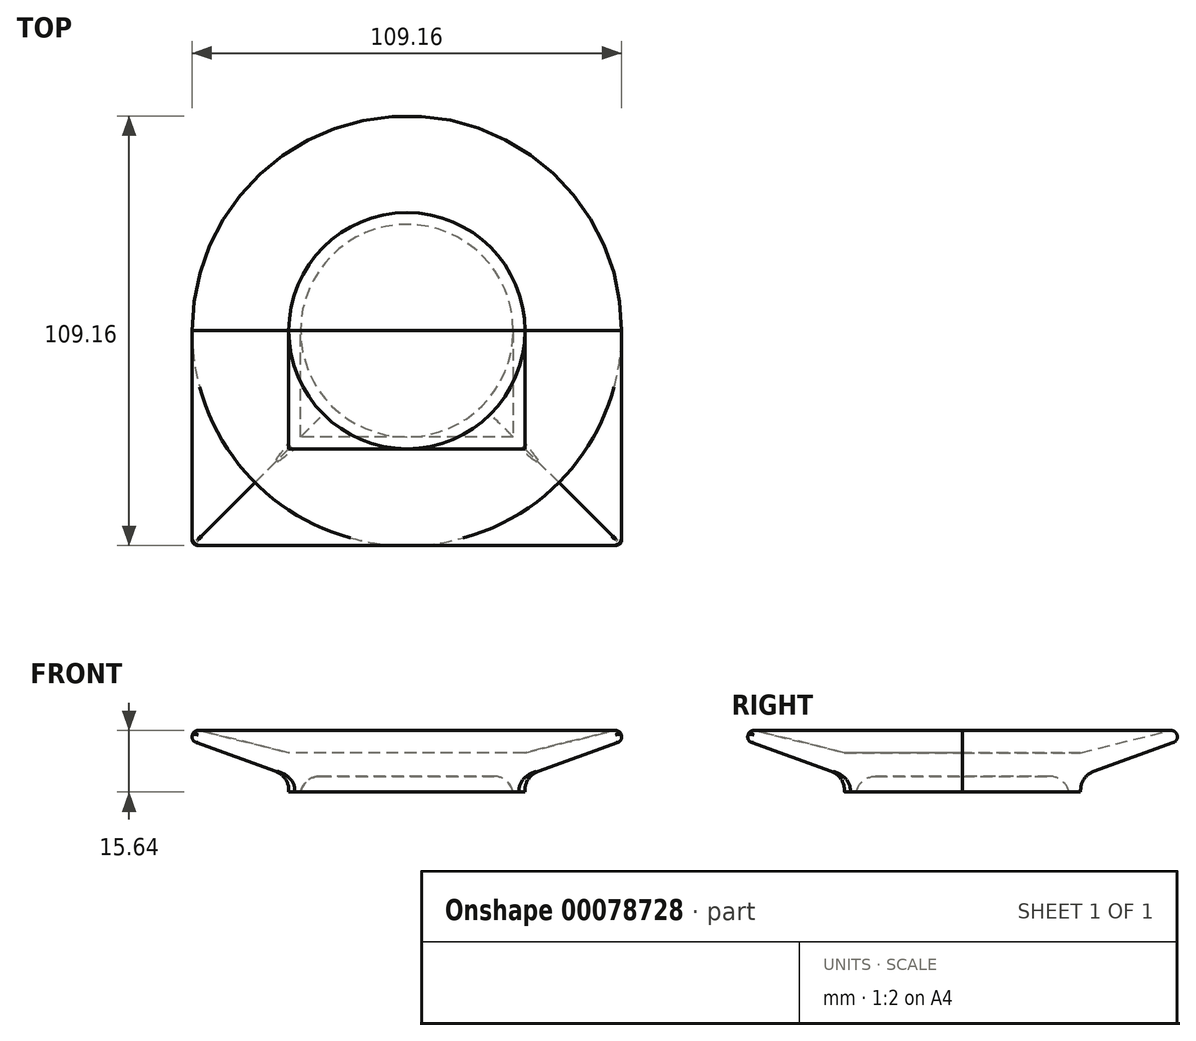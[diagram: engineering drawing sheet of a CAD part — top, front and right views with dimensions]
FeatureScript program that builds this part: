
annotation { "Feature Type Name" : "Feature", "Feature Type Description" : "" }
export const myFeature = defineFeature(function(context is Context, id is Id, definition is map)
    precondition{}
    {
        {
            var Q0;
            Q0=qCreatedBy(makeId("Top.planeOp"),FACE);
            var sketch = newSketch(context, id + "F0", { "sketchPlane" : qUnion([Q0])});
            skLineSegment(sketch, "E0.bottom", {"start": v(30, 30) * mm, "end": v(-30, 30) * mm});
            skLineSegment(sketch, "E0.top", {"start": v(30, -30) * mm, "end": v(-30, -30) * mm});
            skLineSegment(sketch, "E0.left", {"start": v(30, 30) * mm, "end": v(30, -30) * mm});
            skLineSegment(sketch, "E0.right", {"start": v(-30, 30) * mm, "end": v(-30, -30) * mm});
            skPoint(sketch, "E0.middle", {"position": v(0, 0) * mm});
            skSolve(sketch);
        }
        {
            var Q0;
            Q0=makeQuery(id+"F0.imprint","IMPRINT",FACE,{"disambiguationData":[TD([[makeQuery(id+"F0.imprint","IMPRINT",EDGE,{"derivedFrom":sQuery(id+"F0.wireOp",EDGE,"E0.bottom")}),1.0]])]});
            extrude(context, id + "F1", {"entities" : qUnion([Q0]), "depth" : 6 * mm});
        }
        {
            var Q0;
            Q0=qCreatedBy(makeId("Front.planeOp"),FACE);
            var sketch = newSketch(context, id + "F2", { "sketchPlane" : qUnion([Q0])});
            skLineSegment(sketch, "E1.0", {"start": v(30, 6) * mm, "end": v(30, 0) * mm});
            skLineSegment(sketch, "E2", {"start": v(30, 0) * mm, "end": v(55, 0) * mm, "construction": true});
            skLineSegment(sketch, "E3", {"start": v(30, 0) * mm, "end": v(55, 9.1) * mm});
            skLineSegment(sketch, "E4", {"start": v(55, 9.1) * mm, "end": v(53.97, 11.92) * mm});
            skLineSegment(sketch, "E5", {"start": v(53.97, 11.92) * mm, "end": v(30, 6) * mm});
            skLineSegment(sketch, "E6", {"start": v(0, 58.89) * mm, "end": v(0, -59.83) * mm});
            skSolve(sketch);
        }
        {
            var Q0;
            Q0=makeQuery(id+"F2.imprint","IMPRINT",FACE,{"disambiguationData":[TD([[makeQuery(id+"F2.imprint","IMPRINT",EDGE,{"derivedFrom":sQuery(id+"F2.wireOp",EDGE,"E1.0")}),1.0]])]});
            extrude(context, id + "F3", {"entities" : qUnion([Q0]), "endBound" : BoundingType.SYMMETRIC, "depth" : 122.42 * mm});
        }
        {
            var Q0;
            Q0=makeQuery(id+"F3.opExtrude","SWEPT_BODY",BODY,{"disambiguationData":[OSD([sQuery(id+"F2.wireOp",EDGE,"E1.0"),sQuery(id+"F2.wireOp",EDGE,"E3"),sQuery(id+"F2.wireOp",EDGE,"E4"),sQuery(id+"F2.wireOp",EDGE,"E5")])]});
            var Q1;
            Q1=sQuery(id+"F2.wireOp",EDGE,"E6");
            circularPattern(context, id + "F4", {"operationType" : NewBodyOperationType.ADD, "entities" : qUnion([Q0]), "axis" : qUnion([Q1]), "angle" : 360 * degree, "instanceCount" : 4, "equalSpace" : true});
        }
        {
            var Q0;
            Q0=qCreatedBy(makeId("Front.planeOp"),FACE);
            var sketch = newSketch(context, id + "F5", { "sketchPlane" : qUnion([Q0])});
            skLineSegment(sketch, "E7.0", {"start": v(30, 0) * mm, "end": v(55, 9.1) * mm});
            skLineSegment(sketch, "E8.0", {"start": v(55, 9.1) * mm, "end": v(53.97, 11.92) * mm});
            skLineSegment(sketch, "E9", {"start": v(53.97, 11.92) * mm, "end": v(62.12, 21.43) * mm});
            skLineSegment(sketch, "E10", {"start": v(62.12, 21.43) * mm, "end": v(87.77, -20) * mm});
            skLineSegment(sketch, "E11", {"start": v(87.77, -20) * mm, "end": v(30.92, -15.49) * mm});
            skLineSegment(sketch, "E12", {"start": v(30.92, -15.49) * mm, "end": v(30, 0) * mm});
            skSolve(sketch);
        }
        {
            var Q0;
            Q0=makeQuery(id+"F5.imprint","IMPRINT",FACE,{"disambiguationData":[TD([[makeQuery(id+"F5.imprint","IMPRINT",EDGE,{"derivedFrom":sQuery(id+"F5.wireOp",EDGE,"E7.0")}),-1.0]])]});
            extrude(context, id + "F6", {"entities" : qUnion([Q0]), "endBound" : BoundingType.SYMMETRIC, "depth" : 220.76 * mm});
        }
        {
            var Q0;
            Q0=makeQuery(id+"F6.opExtrude","SWEPT_BODY",BODY,{"disambiguationData":[OSD([sQuery(id+"F5.wireOp",EDGE,"E7.0"),sQuery(id+"F5.wireOp",EDGE,"E8.0"),sQuery(id+"F5.wireOp",EDGE,"E9"),sQuery(id+"F5.wireOp",EDGE,"E10"),sQuery(id+"F5.wireOp",EDGE,"E11"),sQuery(id+"F5.wireOp",EDGE,"E12")])]});
            var Q1;
            Q1=sQuery(id+"F2.wireOp",EDGE,"E6");
            circularPattern(context, id + "F7", {"operationType" : NewBodyOperationType.REMOVE, "entities" : qUnion([Q0]), "axis" : qUnion([Q1]), "angle" : 360 * degree, "instanceCount" : 4, "equalSpace" : true});
        }
        {
            var Q0;
            Q0=makeQuery(id+"F1.opExtrude","CAP_FACE",FACE,{"disambiguationData":[OSD([sQuery(id+"F0.wireOp",EDGE,"E0.bottom"),sQuery(id+"F0.wireOp",EDGE,"E0.top"),sQuery(id+"F0.wireOp",EDGE,"E0.left"),sQuery(id+"F0.wireOp",EDGE,"E0.right")])],"isStart":true});
            var sketch = newSketch(context, id + "F8", { "sketchPlane" : qUnion([Q0])});
            skLineSegment(sketch, "E13.0.0", {"start": v(-30, -30) * mm, "end": v(30, -30) * mm});
            skLineSegment(sketch, "E13.0.2", {"start": v(30, -30) * mm, "end": v(30, 30) * mm});
            skLineSegment(sketch, "E13.0.4", {"start": v(30, 30) * mm, "end": v(-30, 30) * mm});
            skLineSegment(sketch, "E13.0.6", {"start": v(-30, 30) * mm, "end": v(-30, -30) * mm});
            skLineSegment(sketch, "E14.0", {"start": v(-27, -27) * mm, "end": v(27, -27) * mm});
            skLineSegment(sketch, "E14.1", {"start": v(-27, 27) * mm, "end": v(-27, -27) * mm});
            skLineSegment(sketch, "E14.2", {"start": v(27, 27) * mm, "end": v(-27, 27) * mm});
            skLineSegment(sketch, "E14.3", {"start": v(27, -27) * mm, "end": v(27, 27) * mm});
            skPoint(sketch, "E15.orphan", {"position": v(30, 43.49) * mm});
            skPoint(sketch, "E16.orphan", {"position": v(-43.49, 30) * mm});
            skPoint(sketch, "E17.orphan", {"position": v(-30, -43.49) * mm});
            skPoint(sketch, "E18.orphan", {"position": v(-43.49, -30) * mm});
            skPoint(sketch, "E19.orphan", {"position": v(-30, -45.08) * mm});
            skPoint(sketch, "E20.orphan", {"position": v(43.49, -30) * mm});
            skPoint(sketch, "E21.orphan", {"position": v(45.17, -30) * mm});
            skSolve(sketch);
        }
        {
            var Q0;
            Q0=makeQuery(id+"F8.imprint","IMPRINT",FACE,{"disambiguationData":[TD([[makeQuery(id+"F8.imprint","IMPRINT",EDGE,{"derivedFrom":sQuery(id+"F8.wireOp",EDGE,"E13.0.0")}),-1.0]])]});
            extrude(context, id + "F9", {"entities" : qUnion([Q0]), "operationType" : NewBodyOperationType.ADD, "depth" : 4 * mm});
        }
        {
            var Q0;
            {var subQ0=sQuery(id+"F2.wireOp",EDGE,"E5");var subQ1=makeQuery(id+"F3.opExtrude","SWEPT_FACE",FACE,{"disambiguationData":[OSD([subQ0])]});var subQ2=sQuery(id+"F2.wireOp",EDGE,"E4");var subQ3=makeQuery(id+"F3.opExtrude","SWEPT_FACE",FACE,{"disambiguationData":[OSD([subQ2])]});Q0=makeQuery(id+"F4.boolean.opBoolean","SPLIT",EDGE,{"disambiguationData":[TD([subQ3,subQ1,makeQuery(id+"F4.opPattern","COPY",FACE,{"derivedFrom":subQ3,"instanceName":"1"}),makeQuery(id+"F4.opPattern","COPY",FACE,{"derivedFrom":subQ1,"instanceName":"1"}),makeQuery(id+"F4.opPattern","COPY",FACE,{"derivedFrom":subQ3,"instanceName":"2"}),makeQuery(id+"F4.opPattern","COPY",FACE,{"derivedFrom":subQ1,"instanceName":"2"})])],"derivedFrom":makeQuery(id+"F4.opPattern","COPY",EDGE,{"derivedFrom":makeQuery(id+"F3.opExtrude","SWEPT_EDGE",EDGE,{"disambiguationData":[OSD([subQ2,subQ0])]}),"instanceName":"1"})});}
            var Q1;
            {var subQ0=sQuery(id+"F2.wireOp",EDGE,"E5");var subQ1=makeQuery(id+"F3.opExtrude","SWEPT_FACE",FACE,{"disambiguationData":[OSD([subQ0])]});var subQ2=sQuery(id+"F2.wireOp",EDGE,"E4");var subQ3=makeQuery(id+"F3.opExtrude","SWEPT_FACE",FACE,{"disambiguationData":[OSD([subQ2])]});Q1=makeQuery(id+"F4.boolean.opBoolean","SPLIT",EDGE,{"disambiguationData":[TD([makeQuery(id+"F4.opPattern","COPY",FACE,{"derivedFrom":subQ3,"instanceName":"1"}),makeQuery(id+"F4.opPattern","COPY",FACE,{"derivedFrom":subQ1,"instanceName":"1"}),makeQuery(id+"F4.opPattern","COPY",FACE,{"derivedFrom":subQ3,"instanceName":"2"}),makeQuery(id+"F4.opPattern","COPY",FACE,{"derivedFrom":subQ1,"instanceName":"2"}),makeQuery(id+"F4.opPattern","COPY",FACE,{"derivedFrom":subQ3,"instanceName":"3"}),makeQuery(id+"F4.opPattern","COPY",FACE,{"derivedFrom":subQ1,"instanceName":"3"})])],"derivedFrom":makeQuery(id+"F4.opPattern","COPY",EDGE,{"derivedFrom":makeQuery(id+"F3.opExtrude","SWEPT_EDGE",EDGE,{"disambiguationData":[OSD([subQ2,subQ0])]}),"instanceName":"2"})});}
            var Q2;
            {var subQ0=sQuery(id+"F2.wireOp",EDGE,"E5");var subQ1=makeQuery(id+"F3.opExtrude","SWEPT_FACE",FACE,{"disambiguationData":[OSD([subQ0])]});var subQ2=sQuery(id+"F2.wireOp",EDGE,"E4");var subQ3=makeQuery(id+"F3.opExtrude","SWEPT_FACE",FACE,{"disambiguationData":[OSD([subQ2])]});Q2=makeQuery(id+"F4.boolean.opBoolean","SPLIT",EDGE,{"disambiguationData":[TD([subQ3,subQ1,makeQuery(id+"F4.opPattern","COPY",FACE,{"derivedFrom":subQ3,"instanceName":"2"}),makeQuery(id+"F4.opPattern","COPY",FACE,{"derivedFrom":subQ1,"instanceName":"2"}),makeQuery(id+"F4.opPattern","COPY",FACE,{"derivedFrom":subQ3,"instanceName":"3"}),makeQuery(id+"F4.opPattern","COPY",FACE,{"derivedFrom":subQ1,"instanceName":"3"})])],"derivedFrom":makeQuery(id+"F4.opPattern","COPY",EDGE,{"derivedFrom":makeQuery(id+"F3.opExtrude","SWEPT_EDGE",EDGE,{"disambiguationData":[OSD([subQ2,subQ0])]}),"instanceName":"3"})});}
            var Q3;
            {var subQ0=sQuery(id+"F2.wireOp",EDGE,"E5");var subQ1=makeQuery(id+"F3.opExtrude","SWEPT_FACE",FACE,{"disambiguationData":[OSD([subQ0])]});var subQ2=sQuery(id+"F2.wireOp",EDGE,"E4");var subQ3=makeQuery(id+"F3.opExtrude","SWEPT_FACE",FACE,{"disambiguationData":[OSD([subQ2])]});Q3=makeQuery(id+"F4.boolean.opBoolean","SPLIT",EDGE,{"disambiguationData":[TD([subQ3,subQ1,makeQuery(id+"F4.opPattern","COPY",FACE,{"derivedFrom":subQ3,"instanceName":"1"}),makeQuery(id+"F4.opPattern","COPY",FACE,{"derivedFrom":subQ1,"instanceName":"1"}),makeQuery(id+"F4.opPattern","COPY",FACE,{"derivedFrom":subQ3,"instanceName":"3"}),makeQuery(id+"F4.opPattern","COPY",FACE,{"derivedFrom":subQ1,"instanceName":"3"})])],"derivedFrom":makeQuery(id+"F3.opExtrude","SWEPT_EDGE",EDGE,{"disambiguationData":[OSD([subQ2,subQ0])]})});}
            var Q4;
            {var subQ0=makeQuery(id+"F3.opExtrude","SWEPT_FACE",FACE,{"disambiguationData":[OSD([sQuery(id+"F2.wireOp",EDGE,"E5")])]});var subQ1=sQuery(id+"F2.wireOp",EDGE,"E3");var subQ2=sQuery(id+"F2.wireOp",EDGE,"E4");Q4=makeQuery(id+"F7.boolean.opBoolean","MERGE",EDGE,{"derivedFrom":[makeQuery(id+"F4.boolean.opBoolean","SPLIT",EDGE,{"disambiguationData":[TD([makeQuery(id+"F4.opPattern","COPY",FACE,{"derivedFrom":subQ0,"instanceName":"1"})])],"derivedFrom":makeQuery(id+"F4.opPattern","COPY",EDGE,{"derivedFrom":makeQuery(id+"F3.opExtrude","SWEPT_EDGE",EDGE,{"disambiguationData":[OSD([subQ1,subQ2])]}),"instanceName":"2"})}),makeQuery(id+"F7.opPattern","COPY",EDGE,{"derivedFrom":makeQuery(id+"F6.opExtrude","SWEPT_EDGE",EDGE,{"disambiguationData":[OSD([sQuery(id+"F5.wireOp",EDGE,"E7.0"),sQuery(id+"F5.wireOp",EDGE,"E8.0")])]}),"instanceName":"2"})]});}
            var Q5;
            {var subQ0=makeQuery(id+"F3.opExtrude","SWEPT_FACE",FACE,{"disambiguationData":[OSD([sQuery(id+"F2.wireOp",EDGE,"E5")])]});var subQ1=sQuery(id+"F2.wireOp",EDGE,"E3");var subQ2=sQuery(id+"F2.wireOp",EDGE,"E4");Q5=makeQuery(id+"F7.boolean.opBoolean","MERGE",EDGE,{"derivedFrom":[makeQuery(id+"F4.boolean.opBoolean","SPLIT",EDGE,{"disambiguationData":[TD([subQ0])],"derivedFrom":makeQuery(id+"F4.opPattern","COPY",EDGE,{"derivedFrom":makeQuery(id+"F3.opExtrude","SWEPT_EDGE",EDGE,{"disambiguationData":[OSD([subQ1,subQ2])]}),"instanceName":"1"})}),makeQuery(id+"F7.opPattern","COPY",EDGE,{"derivedFrom":makeQuery(id+"F6.opExtrude","SWEPT_EDGE",EDGE,{"disambiguationData":[OSD([sQuery(id+"F5.wireOp",EDGE,"E7.0"),sQuery(id+"F5.wireOp",EDGE,"E8.0")])]}),"instanceName":"1"})]});}
            var Q6;
            {var subQ0=sQuery(id+"F2.wireOp",EDGE,"E3");var subQ1=sQuery(id+"F2.wireOp",EDGE,"E4");var subQ2=makeQuery(id+"F3.opExtrude","SWEPT_FACE",FACE,{"disambiguationData":[OSD([sQuery(id+"F2.wireOp",EDGE,"E5")])]});Q6=makeQuery(id+"F7.boolean.opBoolean","MERGE",EDGE,{"derivedFrom":[makeQuery(id+"F4.boolean.opBoolean","SPLIT",EDGE,{"disambiguationData":[TD([makeQuery(id+"F4.opPattern","COPY",FACE,{"derivedFrom":subQ2,"instanceName":"1"})])],"derivedFrom":makeQuery(id+"F3.opExtrude","SWEPT_EDGE",EDGE,{"disambiguationData":[OSD([subQ0,subQ1])]})}),makeQuery(id+"F6.opExtrude","SWEPT_EDGE",EDGE,{"disambiguationData":[OSD([sQuery(id+"F5.wireOp",EDGE,"E7.0"),sQuery(id+"F5.wireOp",EDGE,"E8.0")])]})]});}
            var Q7;
            {var subQ0=makeQuery(id+"F3.opExtrude","SWEPT_FACE",FACE,{"disambiguationData":[OSD([sQuery(id+"F2.wireOp",EDGE,"E5")])]});var subQ1=sQuery(id+"F2.wireOp",EDGE,"E3");var subQ2=sQuery(id+"F2.wireOp",EDGE,"E4");Q7=makeQuery(id+"F7.boolean.opBoolean","MERGE",EDGE,{"derivedFrom":[makeQuery(id+"F4.boolean.opBoolean","SPLIT",EDGE,{"disambiguationData":[TD([subQ0])],"derivedFrom":makeQuery(id+"F4.opPattern","COPY",EDGE,{"derivedFrom":makeQuery(id+"F3.opExtrude","SWEPT_EDGE",EDGE,{"disambiguationData":[OSD([subQ1,subQ2])]}),"instanceName":"3"})}),makeQuery(id+"F7.opPattern","COPY",EDGE,{"derivedFrom":makeQuery(id+"F6.opExtrude","SWEPT_EDGE",EDGE,{"disambiguationData":[OSD([sQuery(id+"F5.wireOp",EDGE,"E7.0"),sQuery(id+"F5.wireOp",EDGE,"E8.0")])]}),"instanceName":"3"})]});}
            fillet(context, id + "F10", {"entities" : qUnion([Q0, Q1, Q2, Q3, Q4, Q5, Q6, Q7]), "radius" : 1.5 * mm, "tangentPropagation" : true, "allowEdgeOverflow" : false});
        }
        {
            var Q0;
            Q0=makeQuery(id+"F1.opExtrude","CAP_FACE",FACE,{"disambiguationData":[OSD([sQuery(id+"F0.wireOp",EDGE,"E0.bottom"),sQuery(id+"F0.wireOp",EDGE,"E0.top"),sQuery(id+"F0.wireOp",EDGE,"E0.left"),sQuery(id+"F0.wireOp",EDGE,"E0.right")])],"isStart":true});
            var Q1;
            Q1=makeQuery(id+"F9.boolean.opBoolean","MERGE",EDGE,{"derivedFrom":[makeQuery(id+"F4.boolean.opBoolean","MERGE",EDGE,{"derivedFrom":[makeQuery(id+"F1.opExtrude","CAP_EDGE",EDGE,{"disambiguationData":[OSD([sQuery(id+"F0.wireOp",EDGE,"E0.left")])],"isStart":true}),makeQuery(id+"F3.opExtrude","SWEPT_EDGE",EDGE,{"disambiguationData":[OSD([sQuery(id+"F2.wireOp",EDGE,"E1.0"),sQuery(id+"F2.wireOp",EDGE,"E3")])]})]}),makeQuery(id+"F9.opExtrude","CAP_EDGE",EDGE,{"disambiguationData":[OSD([sQuery(id+"F8.wireOp",EDGE,"E13.0.2")])],"isStart":true})]});
            var Q2;
            Q2=makeQuery(id+"F9.boolean.opBoolean","MERGE",EDGE,{"derivedFrom":[makeQuery(id+"F4.boolean.opBoolean","MERGE",EDGE,{"derivedFrom":[makeQuery(id+"F1.opExtrude","CAP_EDGE",EDGE,{"disambiguationData":[OSD([sQuery(id+"F0.wireOp",EDGE,"E0.top")])],"isStart":true}),makeQuery(id+"F4.opPattern","COPY",EDGE,{"derivedFrom":makeQuery(id+"F3.opExtrude","SWEPT_EDGE",EDGE,{"disambiguationData":[OSD([sQuery(id+"F2.wireOp",EDGE,"E1.0"),sQuery(id+"F2.wireOp",EDGE,"E3")])]}),"instanceName":"1"})]}),makeQuery(id+"F9.opExtrude","CAP_EDGE",EDGE,{"disambiguationData":[OSD([sQuery(id+"F8.wireOp",EDGE,"E13.0.4")])],"isStart":true})]});
            var Q3;
            Q3=makeQuery(id+"F9.boolean.opBoolean","MERGE",EDGE,{"derivedFrom":[makeQuery(id+"F4.boolean.opBoolean","MERGE",EDGE,{"derivedFrom":[makeQuery(id+"F1.opExtrude","CAP_EDGE",EDGE,{"disambiguationData":[OSD([sQuery(id+"F0.wireOp",EDGE,"E0.right")])],"isStart":true}),makeQuery(id+"F4.opPattern","COPY",EDGE,{"derivedFrom":makeQuery(id+"F3.opExtrude","SWEPT_EDGE",EDGE,{"disambiguationData":[OSD([sQuery(id+"F2.wireOp",EDGE,"E1.0"),sQuery(id+"F2.wireOp",EDGE,"E3")])]}),"instanceName":"2"})]}),makeQuery(id+"F9.opExtrude","CAP_EDGE",EDGE,{"disambiguationData":[OSD([sQuery(id+"F8.wireOp",EDGE,"E13.0.6")])],"isStart":true})]});
            var Q4;
            Q4=makeQuery(id+"F9.boolean.opBoolean","MERGE",EDGE,{"derivedFrom":[makeQuery(id+"F4.boolean.opBoolean","MERGE",EDGE,{"derivedFrom":[makeQuery(id+"F1.opExtrude","CAP_EDGE",EDGE,{"disambiguationData":[OSD([sQuery(id+"F0.wireOp",EDGE,"E0.bottom")])],"isStart":true}),makeQuery(id+"F4.opPattern","COPY",EDGE,{"derivedFrom":makeQuery(id+"F3.opExtrude","SWEPT_EDGE",EDGE,{"disambiguationData":[OSD([sQuery(id+"F2.wireOp",EDGE,"E1.0"),sQuery(id+"F2.wireOp",EDGE,"E3")])]}),"instanceName":"3"})]}),makeQuery(id+"F9.opExtrude","CAP_EDGE",EDGE,{"disambiguationData":[OSD([sQuery(id+"F8.wireOp",EDGE,"E13.0.0")])],"isStart":true})]});
            fillet(context, id + "F11", {"entities" : qUnion([Q0, Q1, Q2, Q3, Q4]), "radius" : 5 * mm, "tangentPropagation" : true, "allowEdgeOverflow" : false});
        }
        {
            var Q0;
            {var subQ0=makeQuery(id+"F6.opExtrude","SWEPT_EDGE",EDGE,{"disambiguationData":[OSD([sQuery(id+"F5.wireOp",EDGE,"E7.0"),sQuery(id+"F5.wireOp",EDGE,"E8.0")])]});var subQ1=makeQuery(id+"F3.opExtrude","SWEPT_FACE",FACE,{"disambiguationData":[OSD([sQuery(id+"F2.wireOp",EDGE,"E5")])]});var subQ2=sQuery(id+"F2.wireOp",EDGE,"E3");var subQ4=sQuery(id+"F2.wireOp",EDGE,"E4");var subQ6=makeQuery(id+"F3.opExtrude","SWEPT_EDGE",EDGE,{"disambiguationData":[OSD([subQ2,subQ4])]});Q0=makeQuery(id+"F10.opFillet","BLEND_EDGE",EDGE,{"blendedFrom":[makeQuery(id+"F7.boolean.opBoolean","MERGE",EDGE,{"derivedFrom":[makeQuery(id+"F4.boolean.opBoolean","SPLIT",EDGE,{"disambiguationData":[TD([subQ1])],"derivedFrom":makeQuery(id+"F4.opPattern","COPY",EDGE,{"derivedFrom":subQ6,"instanceName":"1"})}),makeQuery(id+"F7.opPattern","COPY",EDGE,{"derivedFrom":subQ0,"instanceName":"1"})]}),makeQuery(id+"F7.boolean.opBoolean","MERGE",EDGE,{"derivedFrom":[makeQuery(id+"F4.boolean.opBoolean","SPLIT",EDGE,{"disambiguationData":[TD([makeQuery(id+"F4.opPattern","COPY",FACE,{"derivedFrom":subQ1,"instanceName":"1"})])],"derivedFrom":makeQuery(id+"F4.opPattern","COPY",EDGE,{"derivedFrom":subQ6,"instanceName":"2"})}),makeQuery(id+"F7.opPattern","COPY",EDGE,{"derivedFrom":subQ0,"instanceName":"2"})]})],"blendedInto":[]});}
            var Q1;
            {var subQ0=sQuery(id+"F2.wireOp",EDGE,"E5");var subQ1=makeQuery(id+"F3.opExtrude","SWEPT_FACE",FACE,{"disambiguationData":[OSD([subQ0])]});var subQ2=makeQuery(id+"F4.opPattern","COPY",FACE,{"derivedFrom":subQ1,"instanceName":"2"});var subQ3=sQuery(id+"F2.wireOp",EDGE,"E4");var subQ4=makeQuery(id+"F3.opExtrude","SWEPT_FACE",FACE,{"disambiguationData":[OSD([subQ3])]});var subQ5=makeQuery(id+"F4.opPattern","COPY",FACE,{"derivedFrom":subQ4,"instanceName":"2"});var subQ6=makeQuery(id+"F4.opPattern","COPY",FACE,{"derivedFrom":subQ1,"instanceName":"1"});var subQ7=makeQuery(id+"F4.opPattern","COPY",FACE,{"derivedFrom":subQ4,"instanceName":"1"});var subQ8=makeQuery(id+"F3.opExtrude","SWEPT_EDGE",EDGE,{"disambiguationData":[OSD([subQ3,subQ0])]});Q1=makeQuery(id+"F10.opFillet","BLEND_EDGE",EDGE,{"blendedFrom":[makeQuery(id+"F4.boolean.opBoolean","SPLIT",EDGE,{"disambiguationData":[TD([subQ4,subQ1,subQ7,subQ6,subQ5,subQ2])],"derivedFrom":makeQuery(id+"F4.opPattern","COPY",EDGE,{"derivedFrom":subQ8,"instanceName":"1"})}),makeQuery(id+"F4.boolean.opBoolean","SPLIT",EDGE,{"disambiguationData":[TD([subQ7,subQ6,subQ5,subQ2,makeQuery(id+"F4.opPattern","COPY",FACE,{"derivedFrom":subQ4,"instanceName":"3"}),makeQuery(id+"F4.opPattern","COPY",FACE,{"derivedFrom":subQ1,"instanceName":"3"})])],"derivedFrom":makeQuery(id+"F4.opPattern","COPY",EDGE,{"derivedFrom":subQ8,"instanceName":"2"})})],"blendedInto":[]});}
            var Q2;
            {var subQ0=makeQuery(id+"F6.opExtrude","SWEPT_EDGE",EDGE,{"disambiguationData":[OSD([sQuery(id+"F5.wireOp",EDGE,"E7.0"),sQuery(id+"F5.wireOp",EDGE,"E8.0")])]});var subQ1=makeQuery(id+"F3.opExtrude","SWEPT_FACE",FACE,{"disambiguationData":[OSD([sQuery(id+"F2.wireOp",EDGE,"E5")])]});var subQ2=sQuery(id+"F2.wireOp",EDGE,"E3");var subQ4=sQuery(id+"F2.wireOp",EDGE,"E4");var subQ6=makeQuery(id+"F3.opExtrude","SWEPT_EDGE",EDGE,{"disambiguationData":[OSD([subQ2,subQ4])]});Q2=makeQuery(id+"F10.opFillet","BLEND_EDGE",EDGE,{"blendedFrom":[makeQuery(id+"F7.boolean.opBoolean","MERGE",EDGE,{"derivedFrom":[makeQuery(id+"F4.boolean.opBoolean","SPLIT",EDGE,{"disambiguationData":[TD([makeQuery(id+"F4.opPattern","COPY",FACE,{"derivedFrom":subQ1,"instanceName":"1"})])],"derivedFrom":subQ6}),subQ0]}),makeQuery(id+"F7.boolean.opBoolean","MERGE",EDGE,{"derivedFrom":[makeQuery(id+"F4.boolean.opBoolean","SPLIT",EDGE,{"disambiguationData":[TD([subQ1])],"derivedFrom":makeQuery(id+"F4.opPattern","COPY",EDGE,{"derivedFrom":subQ6,"instanceName":"1"})}),makeQuery(id+"F7.opPattern","COPY",EDGE,{"derivedFrom":subQ0,"instanceName":"1"})]})],"blendedInto":[]});}
            var Q3;
            {var subQ0=sQuery(id+"F2.wireOp",EDGE,"E5");var subQ1=makeQuery(id+"F3.opExtrude","SWEPT_FACE",FACE,{"disambiguationData":[OSD([subQ0])]});var subQ2=makeQuery(id+"F4.opPattern","COPY",FACE,{"derivedFrom":subQ1,"instanceName":"1"});var subQ3=sQuery(id+"F2.wireOp",EDGE,"E4");var subQ4=makeQuery(id+"F3.opExtrude","SWEPT_FACE",FACE,{"disambiguationData":[OSD([subQ3])]});var subQ5=makeQuery(id+"F4.opPattern","COPY",FACE,{"derivedFrom":subQ4,"instanceName":"1"});var subQ6=makeQuery(id+"F3.opExtrude","SWEPT_EDGE",EDGE,{"disambiguationData":[OSD([subQ3,subQ0])]});Q3=makeQuery(id+"F10.opFillet","BLEND_EDGE",EDGE,{"blendedFrom":[makeQuery(id+"F4.boolean.opBoolean","SPLIT",EDGE,{"disambiguationData":[TD([subQ4,subQ1,subQ5,subQ2,makeQuery(id+"F4.opPattern","COPY",FACE,{"derivedFrom":subQ4,"instanceName":"3"}),makeQuery(id+"F4.opPattern","COPY",FACE,{"derivedFrom":subQ1,"instanceName":"3"})])],"derivedFrom":subQ6}),makeQuery(id+"F4.boolean.opBoolean","SPLIT",EDGE,{"disambiguationData":[TD([subQ4,subQ1,subQ5,subQ2,makeQuery(id+"F4.opPattern","COPY",FACE,{"derivedFrom":subQ4,"instanceName":"2"}),makeQuery(id+"F4.opPattern","COPY",FACE,{"derivedFrom":subQ1,"instanceName":"2"})])],"derivedFrom":makeQuery(id+"F4.opPattern","COPY",EDGE,{"derivedFrom":subQ6,"instanceName":"1"})})],"blendedInto":[]});}
            var Q4;
            {var subQ0=sQuery(id+"F2.wireOp",EDGE,"E5");var subQ1=makeQuery(id+"F3.opExtrude","SWEPT_FACE",FACE,{"disambiguationData":[OSD([subQ0])]});var subQ2=sQuery(id+"F2.wireOp",EDGE,"E4");var subQ3=makeQuery(id+"F3.opExtrude","SWEPT_FACE",FACE,{"disambiguationData":[OSD([subQ2])]});var subQ4=makeQuery(id+"F4.opPattern","COPY",FACE,{"derivedFrom":subQ3,"instanceName":"3"});var subQ5=makeQuery(id+"F4.opPattern","COPY",FACE,{"derivedFrom":subQ1,"instanceName":"3"});var subQ6=makeQuery(id+"F3.opExtrude","SWEPT_EDGE",EDGE,{"disambiguationData":[OSD([subQ2,subQ0])]});Q4=makeQuery(id+"F10.opFillet","BLEND_EDGE",EDGE,{"blendedFrom":[makeQuery(id+"F4.boolean.opBoolean","SPLIT",EDGE,{"disambiguationData":[TD([subQ3,subQ1,makeQuery(id+"F4.opPattern","COPY",FACE,{"derivedFrom":subQ3,"instanceName":"1"}),makeQuery(id+"F4.opPattern","COPY",FACE,{"derivedFrom":subQ1,"instanceName":"1"}),subQ4,subQ5])],"derivedFrom":subQ6}),makeQuery(id+"F4.boolean.opBoolean","SPLIT",EDGE,{"disambiguationData":[TD([subQ3,subQ1,makeQuery(id+"F4.opPattern","COPY",FACE,{"derivedFrom":subQ3,"instanceName":"2"}),makeQuery(id+"F4.opPattern","COPY",FACE,{"derivedFrom":subQ1,"instanceName":"2"}),subQ4,subQ5])],"derivedFrom":makeQuery(id+"F4.opPattern","COPY",EDGE,{"derivedFrom":subQ6,"instanceName":"3"})})],"blendedInto":[]});}
            var Q5;
            {var subQ0=sQuery(id+"F2.wireOp",EDGE,"E5");var subQ1=makeQuery(id+"F3.opExtrude","SWEPT_FACE",FACE,{"disambiguationData":[OSD([subQ0])]});var subQ2=makeQuery(id+"F4.opPattern","COPY",FACE,{"derivedFrom":subQ1,"instanceName":"2"});var subQ3=sQuery(id+"F2.wireOp",EDGE,"E4");var subQ4=makeQuery(id+"F3.opExtrude","SWEPT_FACE",FACE,{"disambiguationData":[OSD([subQ3])]});var subQ5=makeQuery(id+"F4.opPattern","COPY",FACE,{"derivedFrom":subQ4,"instanceName":"3"});var subQ6=makeQuery(id+"F4.opPattern","COPY",FACE,{"derivedFrom":subQ4,"instanceName":"2"});var subQ7=makeQuery(id+"F4.opPattern","COPY",FACE,{"derivedFrom":subQ1,"instanceName":"3"});var subQ8=makeQuery(id+"F3.opExtrude","SWEPT_EDGE",EDGE,{"disambiguationData":[OSD([subQ3,subQ0])]});Q5=makeQuery(id+"F10.opFillet","BLEND_EDGE",EDGE,{"blendedFrom":[makeQuery(id+"F4.boolean.opBoolean","SPLIT",EDGE,{"disambiguationData":[TD([makeQuery(id+"F4.opPattern","COPY",FACE,{"derivedFrom":subQ4,"instanceName":"1"}),makeQuery(id+"F4.opPattern","COPY",FACE,{"derivedFrom":subQ1,"instanceName":"1"}),subQ6,subQ2,subQ5,subQ7])],"derivedFrom":makeQuery(id+"F4.opPattern","COPY",EDGE,{"derivedFrom":subQ8,"instanceName":"2"})}),makeQuery(id+"F4.boolean.opBoolean","SPLIT",EDGE,{"disambiguationData":[TD([subQ4,subQ1,subQ6,subQ2,subQ5,subQ7])],"derivedFrom":makeQuery(id+"F4.opPattern","COPY",EDGE,{"derivedFrom":subQ8,"instanceName":"3"})})],"blendedInto":[]});}
            fillet(context, id + "F12", {"entities" : qUnion([Q0, Q1, Q2, Q3, Q4, Q5]), "radius" : 1.5 * mm, "tangentPropagation" : true, "allowEdgeOverflow" : false});
        }
        {
            var Q0;
            Q0=qCreatedBy(makeId("Front.planeOp"),FACE);
            var sketch = newSketch(context, id + "F13", { "sketchPlane" : qUnion([Q0])});
            skLineSegment(sketch, "E22.bottom", {"start": v(-135.06, 80.13) * mm, "end": v(146.5, 80.13) * mm});
            skLineSegment(sketch, "E22.top", {"start": v(-135.06, -61.62) * mm, "end": v(146.5, -61.62) * mm});
            skLineSegment(sketch, "E22.left", {"start": v(-135.06, 80.13) * mm, "end": v(-135.06, -61.62) * mm});
            skLineSegment(sketch, "E22.right", {"start": v(146.5, 80.13) * mm, "end": v(146.5, -61.62) * mm});
            skSolve(sketch);
        }
        {
            var Q0;
            Q0=makeQuery(id+"F13.imprint","IMPRINT",FACE,{"disambiguationData":[TD([[makeQuery(id+"F13.imprint","IMPRINT",EDGE,{"derivedFrom":sQuery(id+"F13.wireOp",EDGE,"E22.bottom")}),-1.0]])]});
            extrude(context, id + "F14", {"entities" : qUnion([Q0]), "operationType" : NewBodyOperationType.REMOVE, "oppositeDirection" : true, "depth" : 93.62 * mm});
        }
        {
            var Q0;
            Q0=makeQuery(id+"F14.boolean.opBoolean","COPY",FACE,{"derivedFrom":makeQuery(id+"F14.opExtrude","CAP_FACE",FACE,{"disambiguationData":[OSD([sQuery(id+"F13.wireOp",EDGE,"E22.bottom"),sQuery(id+"F13.wireOp",EDGE,"E22.top"),sQuery(id+"F13.wireOp",EDGE,"E22.left"),sQuery(id+"F13.wireOp",EDGE,"E22.right")])],"isStart":true})});
            var sketch = newSketch(context, id + "F15", { "sketchPlane" : qUnion([Q0])});
            skLineSegment(sketch, "E23", {"start": v(0, 31.36) * mm, "end": v(0, -35.83) * mm});
            skArc(sketch, "E24.0.0", {"start": v(-54.49, 10.5) * mm, "mid": v(-54.44, 9.36) * mm, "end": v(-53.6, 8.59) * mm});
            skLineSegment(sketch, "E24.0.1", {"start": v(-53.6, 8.59) * mm, "end": v(-33.29, 1.2) * mm});
            skArc(sketch, "E24.0.2", {"start": v(-30, -3.5) * mm, "mid": v(-30.9, -0.63) * mm, "end": v(-33.29, 1.2) * mm});
            skLineSegment(sketch, "E24.0.3", {"start": v(-30, -3.5) * mm, "end": v(-30, -4) * mm});
            skLineSegment(sketch, "E24.0.4", {"start": v(-30, -4) * mm, "end": v(-27, -4) * mm});
            skArc(sketch, "E24.0.5", {"start": v(-22.1, 0) * mm, "mid": v(-25.26, -1.13) * mm, "end": v(-27, -4) * mm});
            skLineSegment(sketch, "E24.0.6", {"start": v(-22.1, 0) * mm, "end": v(22.1, 0) * mm});
            skArc(sketch, "E24.0.7", {"start": v(27, -4) * mm, "mid": v(25.26, -1.13) * mm, "end": v(22.1, 0) * mm});
            skLineSegment(sketch, "E24.0.8", {"start": v(27, -4) * mm, "end": v(30, -4) * mm});
            skLineSegment(sketch, "E24.0.9", {"start": v(30, -4) * mm, "end": v(30, -3.5) * mm});
            skArc(sketch, "E24.0.10", {"start": v(33.29, 1.2) * mm, "mid": v(30.9, -0.63) * mm, "end": v(30, -3.5) * mm});
            skLineSegment(sketch, "E24.0.11", {"start": v(33.29, 1.2) * mm, "end": v(53.6, 8.59) * mm});
            skArc(sketch, "E24.0.12", {"start": v(53.6, 8.59) * mm, "mid": v(54.44, 9.36) * mm, "end": v(54.49, 10.5) * mm});
            skLineSegment(sketch, "E24.0.13", {"start": v(54.49, 10.5) * mm, "end": v(54.43, 10.65) * mm});
            skArc(sketch, "E24.0.14", {"start": v(54.43, 10.65) * mm, "mid": v(53.73, 11.46) * mm, "end": v(52.67, 11.6) * mm});
            skLineSegment(sketch, "E24.0.15", {"start": v(52.67, 11.6) * mm, "end": v(30, 6) * mm});
            skLineSegment(sketch, "E24.0.16", {"start": v(30, 6) * mm, "end": v(-30, 6) * mm});
            skLineSegment(sketch, "E24.0.17", {"start": v(-30, 6) * mm, "end": v(-52.67, 11.6) * mm});
            skArc(sketch, "E24.0.18", {"start": v(-52.67, 11.6) * mm, "mid": v(-53.73, 11.46) * mm, "end": v(-54.43, 10.65) * mm});
            skLineSegment(sketch, "E24.0.19", {"start": v(-54.43, 10.65) * mm, "end": v(-54.49, 10.5) * mm});
            skSolve(sketch);
        }
        {
            var Q0;
            {var subQ0=sQuery(id+"F15.wireOp",EDGE,"E24.0.7");Q0=makeQuery(id+"F15.imprint","IMPRINT",FACE,{"disambiguationData":[TD([[makeQuery(id+"F15.imprint","IMPRINT",EDGE,{"derivedFrom":subQ0}),-1.0]])]});}
            var Q1;
            Q1=sQuery(id+"F15.wireOp",EDGE,"E23");
            revolve(context, id + "F16", {"entities" : qUnion([Q0]), "axis" : qUnion([Q1]), "revolveType" : RevolveType.FULL});
        }
    });
